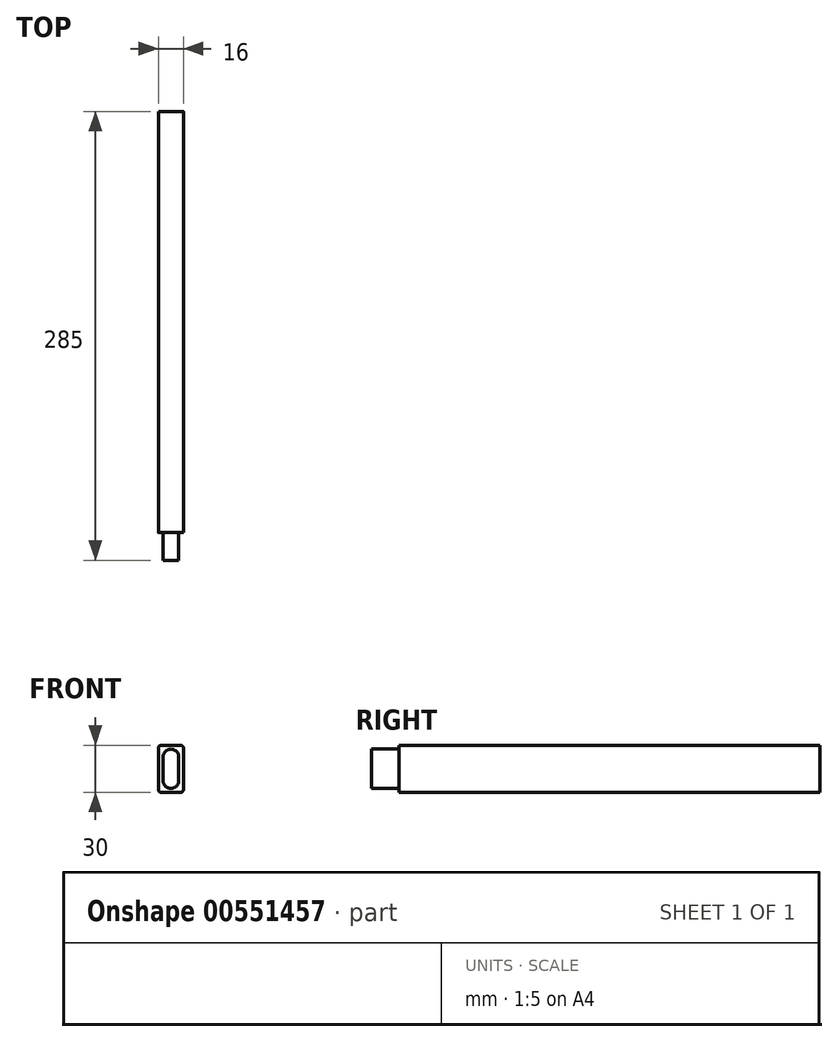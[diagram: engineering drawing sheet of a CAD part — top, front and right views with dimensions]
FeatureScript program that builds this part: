
annotation { "Feature Type Name" : "Feature", "Feature Type Description" : "" }
export const myFeature = defineFeature(function(context is Context, id is Id, definition is map)
    precondition{}
    {
        {
            var Q0;
            Q0=qCreatedBy(makeId("Front.planeOp"),FACE);
            var sketch = newSketch(context, id + "F0", { "sketchPlane" : qUnion([Q0])});
            skLineSegment(sketch, "E0.bottom", {"start": v(-8, -15) * mm, "end": v(8, -15) * mm});
            skLineSegment(sketch, "E0.top", {"start": v(-8, 15) * mm, "end": v(8, 15) * mm});
            skLineSegment(sketch, "E0.left", {"start": v(-8, -15) * mm, "end": v(-8, 15) * mm});
            skLineSegment(sketch, "E0.right", {"start": v(8, -15) * mm, "end": v(8, 15) * mm});
            skPoint(sketch, "E0.middle", {"position": v(0, 0) * mm});
            skSolve(sketch);
        }
        {
            var Q0;
            Q0 = qSketchRegion(id + "F0", true);
            extrude(context, id + "F1", {"entities" : qUnion([Q0]), "depth" : 142.5 * mm, "offsetDistance" : 25 * mm, "hasSecondDirection" : true, "secondDirectionOppositeDirection" : true, "secondDirectionDepth" : 142.5 * mm});
        }
        {
            var Q0;
            Q0=makeQuery(id+"F1.opExtrude","CAP_FACE",FACE,{"disambiguationData":[OSD([sQuery(id+"F0.wireOp",EDGE,"E0.bottom"),sQuery(id+"F0.wireOp",EDGE,"E0.top"),sQuery(id+"F0.wireOp",EDGE,"E0.left"),sQuery(id+"F0.wireOp",EDGE,"E0.right")])],"isStart":false});
            var sketch = newSketch(context, id + "F2", { "sketchPlane" : qUnion([Q0])});
            skLineSegment(sketch, "E1.bottom", {"start": v(-5, -7.5) * mm, "end": v(5, -7.5) * mm});
            skLineSegment(sketch, "E1.top", {"start": v(-5, 7.5) * mm, "end": v(5, 7.5) * mm});
            skLineSegment(sketch, "E1.left", {"start": v(-5, -7.5) * mm, "end": v(-5, 7.5) * mm});
            skLineSegment(sketch, "E1.right", {"start": v(5, -7.5) * mm, "end": v(5, 7.5) * mm});
            skPoint(sketch, "E1.middle", {"position": v(0, 0) * mm});
            skCircle(sketch, "E2", {"center": v(0, 7.5) * mm, "radius": 5 * mm});
            skCircle(sketch, "E3", {"center": v(0, -7.5) * mm, "radius": 5 * mm});
            skLineSegment(sketch, "E4.0.0", {"start": v(8, 15) * mm, "end": v(-8, 15) * mm});
            skLineSegment(sketch, "E4.0.1", {"start": v(-8, 15) * mm, "end": v(-8, -15) * mm});
            skLineSegment(sketch, "E4.0.2", {"start": v(-8, -15) * mm, "end": v(8, -15) * mm});
            skLineSegment(sketch, "E4.0.3", {"start": v(8, -15) * mm, "end": v(8, 15) * mm});
            skSolve(sketch);
        }
        {
            var Q0;
            {var subQ1=sQuery(id+"F2.wireOp",EDGE,"E1.left");Q0=makeQuery(id+"F2.imprint","IMPRINT",FACE,{"disambiguationData":[TD([[makeQuery(id+"F2.imprint","IMPRINT",EDGE,{"derivedFrom":subQ1}),1.0]])]});}
            extrude(context, id + "F3", {"entities" : qUnion([Q0]), "operationType" : NewBodyOperationType.REMOVE, "oppositeDirection" : true, "depth" : 17.5 * mm, "offsetDistance" : 25 * mm});
        }
        {
            var Q0;
            Q0=makeQuery(id+"F1.opExtrude","SWEPT_EDGE",EDGE,{"disambiguationData":[OSD([sQuery(id+"F0.wireOp",EDGE,"E0.top"),sQuery(id+"F0.wireOp",EDGE,"E0.left")])]});
            var Q1;
            Q1=makeQuery(id+"F1.opExtrude","SWEPT_EDGE",EDGE,{"disambiguationData":[OSD([sQuery(id+"F0.wireOp",EDGE,"E0.top"),sQuery(id+"F0.wireOp",EDGE,"E0.right")])]});
            var Q2;
            Q2=makeQuery(id+"F1.opExtrude","SWEPT_EDGE",EDGE,{"disambiguationData":[OSD([sQuery(id+"F0.wireOp",EDGE,"E0.bottom"),sQuery(id+"F0.wireOp",EDGE,"E0.right")])]});
            var Q3;
            Q3=makeQuery(id+"F1.opExtrude","SWEPT_EDGE",EDGE,{"disambiguationData":[OSD([sQuery(id+"F0.wireOp",EDGE,"E0.bottom"),sQuery(id+"F0.wireOp",EDGE,"E0.left")])]});
            fillet(context, id + "F4", {"entities" : qUnion([Q0, Q1, Q2, Q3]), "radius" : 2 * mm, "tangentPropagation" : true, "allowEdgeOverflow" : false});
        }
    });
